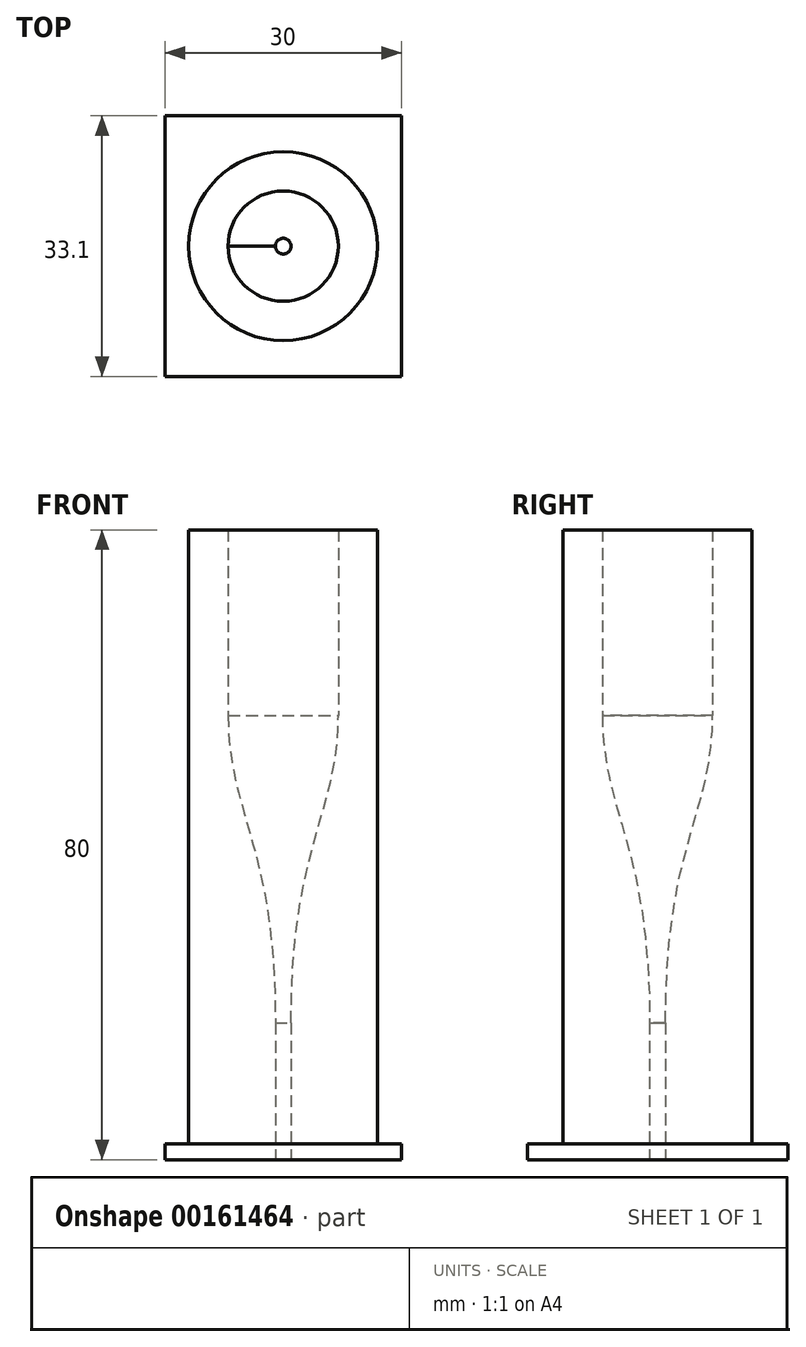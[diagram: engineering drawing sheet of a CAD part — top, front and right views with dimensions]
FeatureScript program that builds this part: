
annotation { "Feature Type Name" : "Feature", "Feature Type Description" : "" }
export const myFeature = defineFeature(function(context is Context, id is Id, definition is map)
    precondition{}
    {
        {
            var Q0;
            Q0=qCreatedBy(makeId("Top.planeOp"),FACE);
            var sketch = newSketch(context, id + "F0", { "sketchPlane" : qUnion([Q0])});
            skLineSegment(sketch, "E0.bottom", {"start": v(15, 16.55) * mm, "end": v(-15, 16.55) * mm});
            skLineSegment(sketch, "E0.top", {"start": v(15, -16.55) * mm, "end": v(-15, -16.55) * mm});
            skLineSegment(sketch, "E0.left", {"start": v(15, 16.55) * mm, "end": v(15, -16.55) * mm});
            skLineSegment(sketch, "E0.right", {"start": v(-15, 16.55) * mm, "end": v(-15, -16.55) * mm});
            skPoint(sketch, "E0.middle", {"position": v(0, 0) * mm});
            skSolve(sketch);
        }
        {
            var Q0;
            Q0=makeQuery(id+"F0.imprint","IMPRINT",FACE,{"disambiguationData":[TD([[makeQuery(id+"F0.imprint","IMPRINT",EDGE,{"derivedFrom":sQuery(id+"F0.wireOp",EDGE,"E0.bottom")}),1.0]])]});
            extrude(context, id + "F1", {"entities" : qUnion([Q0]), "depth" : 2 * mm});
        }
        {
            var Q0;
            Q0=qCreatedBy(makeId("Front.planeOp"),FACE);
            var sketch = newSketch(context, id + "F2", { "sketchPlane" : qUnion([Q0])});
            skLineSegment(sketch, "E1", {"start": v(0, 80) * mm, "end": v(12, 80) * mm});
            skLineSegment(sketch, "E2", {"start": v(12, 80) * mm, "end": v(12, 2) * mm});
            skLineSegment(sketch, "E3", {"start": v(0, 0) * mm, "end": v(0, 80) * mm, "construction": true});
            skLineSegment(sketch, "E4", {"start": v(12, 2) * mm, "end": v(0, 2) * mm});
            skLineSegment(sketch, "E5", {"start": v(0, 2) * mm, "end": v(0, 80) * mm});
            skSolve(sketch);
        }
        {
            var Q0;
            Q0=makeQuery(id+"F2.imprint","IMPRINT",FACE,{"disambiguationData":[TD([[makeQuery(id+"F2.imprint","IMPRINT",EDGE,{"derivedFrom":sQuery(id+"F2.wireOp",EDGE,"E1")}),-1.0]])]});
            var Q1;
            Q1=sQuery(id+"F2.wireOp",EDGE,"010c6d28-2f4e-43ce-9618-e5f15e5f76ce");
            var Q2;
            Q2=sQuery(id+"F2.wireOp",EDGE,"E3");
            revolve(context, id + "F3", {"operationType" : NewBodyOperationType.ADD, "entities" : qUnion([Q0]), "surfaceEntities" : qUnion([Q1]), "axis" : qUnion([Q2]), "revolveType" : RevolveType.FULL});
        }
        {
            var Q0;
            Q0=qCreatedBy(makeId("Front.planeOp"),FACE);
            var sketch = newSketch(context, id + "F4", { "sketchPlane" : qUnion([Q0])});
            skLineSegment(sketch, "E6", {"start": v(0, 80) * mm, "end": v(0, 0) * mm});
            skLineSegment(sketch, "E7", {"start": v(0, 0) * mm, "end": v(-1, 0) * mm});
            skLineSegment(sketch, "E8", {"start": v(-7, 80) * mm, "end": v(0, 80) * mm});
            skLineSegment(sketch, "E9", {"start": v(-1, 0) * mm, "end": v(-1, 17.39) * mm});
            skLineSegment(sketch, "E10", {"start": v(-7, 80) * mm, "end": v(-7, 56.44) * mm});
            skFitSpline(sketch, "E11", {"points": [v(-7, 56.44) * mm, v(-1, 17.39) * mm], "startDerivative": vector(0, -37.6) * mm, "endDerivative": vector(0, -67.84) * mm});
            skSolve(sketch);
        }
        {
            var Q0;
            Q0 = qSketchRegion(id + "F4", true);
            var Q1;
            Q1=sQuery(id+"F4.wireOp",EDGE,"E6");
            revolve(context, id + "F5", {"operationType" : NewBodyOperationType.REMOVE, "entities" : qUnion([Q0]), "axis" : qUnion([Q1]), "revolveType" : RevolveType.FULL, "oppositeDirection" : true});
        }
    });
